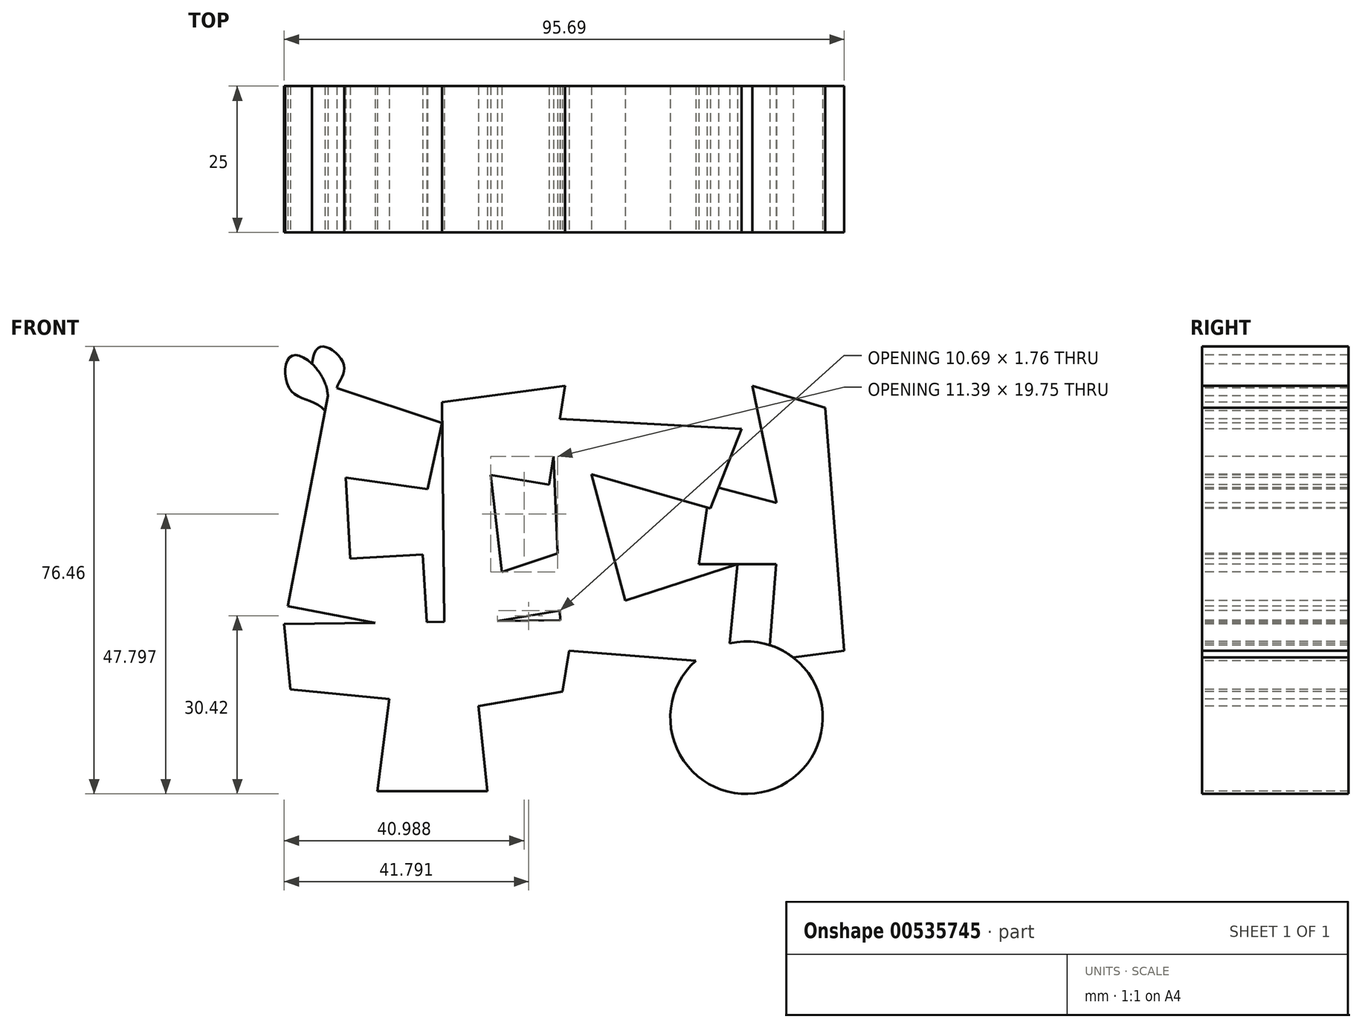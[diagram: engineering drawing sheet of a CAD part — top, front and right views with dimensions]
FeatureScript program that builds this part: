
annotation { "Feature Type Name" : "Feature", "Feature Type Description" : "" }
export const myFeature = defineFeature(function(context is Context, id is Id, definition is map)
    precondition{}
    {
        {
            var Q0;
            Q0=qCreatedBy(makeId("Front.planeOp"),FACE);
            var sketch = newSketch(context, id + "F0", { "sketchPlane" : qUnion([Q0])});
            skLineSegment(sketch, "E0", {"start": v(-48.77, 25.53) * mm, "end": v(-29.6, 19.19) * mm});
            skLineSegment(sketch, "E1", {"start": v(-29.6, 19.19) * mm, "end": v(-32.08, 7.86) * mm});
            skLineSegment(sketch, "E2", {"start": v(-32.08, 7.86) * mm, "end": v(-46.06, 9.88) * mm});
            skLineSegment(sketch, "E3", {"start": v(-46.06, 9.88) * mm, "end": v(-45.24, -3.98) * mm});
            skLineSegment(sketch, "E4", {"start": v(-45.24, -3.98) * mm, "end": v(-32.87, -3.26) * mm});
            skLineSegment(sketch, "E5", {"start": v(-32.87, -3.26) * mm, "end": v(-32.08, -16.68) * mm});
            skLineSegment(sketch, "E6", {"start": v(-32.08, -16.68) * mm, "end": v(-55.94, -12.09) * mm});
            skLineSegment(sketch, "E7", {"start": v(-55.94, -12.09) * mm, "end": v(-48.77, 25.53) * mm});
            skLineSegment(sketch, "E8", {"start": v(-29.6, 22.78) * mm, "end": v(-8.55, 25.53) * mm});
            skLineSegment(sketch, "E9", {"start": v(-8.55, 25.53) * mm, "end": v(-11.3, 8.66) * mm});
            skLineSegment(sketch, "E10", {"start": v(-11.3, 8.66) * mm, "end": v(-21.26, 10.28) * mm});
            skLineSegment(sketch, "E11", {"start": v(-21.26, 10.28) * mm, "end": v(-19.34, -6.27) * mm});
            skLineSegment(sketch, "E12", {"start": v(-19.34, -6.27) * mm, "end": v(-8.5, -2.66) * mm});
            skLineSegment(sketch, "E13", {"start": v(-8.5, -2.66) * mm, "end": v(-9.1, -12.83) * mm});
            skLineSegment(sketch, "E14", {"start": v(-9.1, -12.83) * mm, "end": v(-29.17, -16.15) * mm});
            skLineSegment(sketch, "E15", {"start": v(-29.17, -16.15) * mm, "end": v(-29.6, 22.78) * mm});
            skLineSegment(sketch, "E16", {"start": v(-56.55, -15.18) * mm, "end": v(-7, -14.46) * mm});
            skLineSegment(sketch, "E17", {"start": v(-7, -14.46) * mm, "end": v(-9.02, -26.72) * mm});
            skLineSegment(sketch, "E18", {"start": v(-9.02, -26.72) * mm, "end": v(-23.36, -29.22) * mm});
            skLineSegment(sketch, "E19", {"start": v(-23.36, -29.22) * mm, "end": v(-21.8, -43.75) * mm});
            skLineSegment(sketch, "E20", {"start": v(-21.8, -43.75) * mm, "end": v(-40.65, -43.75) * mm});
            skLineSegment(sketch, "E21", {"start": v(-40.65, -43.75) * mm, "end": v(-38.62, -27.96) * mm});
            skLineSegment(sketch, "E22", {"start": v(-38.62, -27.96) * mm, "end": v(-55.52, -26.34) * mm});
            skLineSegment(sketch, "E23", {"start": v(-55.52, -26.34) * mm, "end": v(-56.55, -15.18) * mm});
            skLineSegment(sketch, "E24", {"start": v(-10.77, 19.93) * mm, "end": v(21.63, 18.2) * mm});
            skLineSegment(sketch, "E25", {"start": v(21.63, 18.2) * mm, "end": v(16.25, 4.58) * mm});
            skLineSegment(sketch, "E26", {"start": v(16.25, 4.58) * mm, "end": v(-4.05, 10.42) * mm});
            skLineSegment(sketch, "E27", {"start": v(-4.05, 10.42) * mm, "end": v(1.7, -11.17) * mm});
            skLineSegment(sketch, "E28", {"start": v(1.7, -11.17) * mm, "end": v(20.91, -4.96) * mm});
            skLineSegment(sketch, "E29", {"start": v(20.91, -4.96) * mm, "end": v(19.26, -21.87) * mm});
            skLineSegment(sketch, "E30", {"start": v(19.26, -21.87) * mm, "end": v(-9.21, -19.65) * mm});
            skLineSegment(sketch, "E31", {"start": v(-9.21, -19.65) * mm, "end": v(-10.77, 19.93) * mm});
            skLineSegment(sketch, "E32", {"start": v(16.25, 8.48) * mm, "end": v(27.6, 5.55) * mm});
            skLineSegment(sketch, "E33", {"start": v(27.6, 5.55) * mm, "end": v(23.43, 25.53) * mm});
            skLineSegment(sketch, "E34", {"start": v(23.43, 25.53) * mm, "end": v(35.87, 21.81) * mm});
            skLineSegment(sketch, "E35", {"start": v(35.87, 21.81) * mm, "end": v(39.14, -19.72) * mm});
            skLineSegment(sketch, "E36", {"start": v(39.14, -19.72) * mm, "end": v(26.22, -21.42) * mm});
            skLineSegment(sketch, "E37", {"start": v(26.22, -21.42) * mm, "end": v(27.51, -4.96) * mm});
            skLineSegment(sketch, "E38", {"start": v(27.51, -4.96) * mm, "end": v(14.3, -4.96) * mm});
            skLineSegment(sketch, "E39", {"start": v(14.3, -4.96) * mm, "end": v(16.25, 8.48) * mm});
            skCircle(sketch, "E40", {"center": v(22.44, -31.17) * mm, "radius": 13.02 * mm});
            skPoint(sketch, "E40.first.point", {"position": v(13.8, -21.44) * mm});
            skPoint(sketch, "E40.second.point", {"position": v(30.77, -41.18) * mm});
            skPoint(sketch, "E40.third.point", {"position": v(35.4, -29.89) * mm});
            skFitSpline(sketch, "E41", {"points": [v(-49.58, 21.3) * mm, v(-55.43, 24.76) * mm, v(-55.25, 30.67) * mm, v(-49.1, 23.85) * mm], "startDerivative": vector(-14.77, 18.4) * mm, "endDerivative": vector(1.75, -32.2) * mm});
            skFitSpline(sketch, "E42", {"points": [v(-49.14, 24.33) * mm, v(-51.56, 26.93) * mm, v(-50.39, 32.21) * mm, v(-46.31, 28.88) * mm, v(-47.66, 24.57) * mm], "startDerivative": vector(-13.77, 8.04) * mm, "endDerivative": vector(-0.25, -17.6) * mm});
            skSolve(sketch);
        }
        {
            var Q0;
            Q0=makeQuery(id+"F0.imprint","IMPRINT",FACE,{"disambiguationData":[TD([[makeQuery(id+"F0.imprint","IMPRINT",EDGE,{"derivedFrom":sQuery(id+"F0.wireOp",EDGE,"E0")}),-1.0]])]});
            var Q1;
            {var subQ1=sQuery(id+"F0.wireOp",EDGE,"E8");Q1=makeQuery(id+"F0.imprint","IMPRINT",FACE,{"disambiguationData":[TD([[makeQuery(id+"F0.imprint","IMPRINT",EDGE,{"derivedFrom":subQ1}),-1.0]])]});}
            var Q2;
            {var subQ0=sQuery(id+"F0.wireOp",EDGE,"E26");var subQ1=sQuery(id+"F0.wireOp",EDGE,"E25");var subQ2=makeQuery(id+"F0.imprint","INTERSECT",VERTEX,{"derivedFrom":[subQ1,subQ0]});Q2=makeQuery(id+"F0.imprint","IMPRINT",FACE,{"disambiguationData":[TD([[makeQuery(id+"F0.imprint","IMPRINT",EDGE,{"disambiguationData":[TD([[subQ2,1.0]])],"derivedFrom":subQ1}),-1.0]])]});}
            var Q3;
            {var subQ0=sQuery(id+"F0.wireOp",EDGE,"E18");Q3=makeQuery(id+"F0.imprint","IMPRINT",FACE,{"disambiguationData":[TD([[makeQuery(id+"F0.imprint","IMPRINT",EDGE,{"derivedFrom":subQ0}),-1.0]])]});}
            var Q4;
            {var subQ0=sQuery(id+"F0.wireOp",EDGE,"E6");var subQ1=sQuery(id+"F0.wireOp",EDGE,"E5");var subQ2=makeQuery(id+"F0.imprint","INTERSECT",VERTEX,{"derivedFrom":[subQ1,subQ0]});Q4=makeQuery(id+"F0.imprint","IMPRINT",FACE,{"disambiguationData":[TD([[makeQuery(id+"F0.imprint","IMPRINT",EDGE,{"disambiguationData":[TD([[subQ2,1.0]])],"derivedFrom":subQ1}),-1.0]])]});}
            var Q5;
            {var subQ0=sQuery(id+"F0.wireOp",EDGE,"E17");var subQ1=sQuery(id+"F0.wireOp",EDGE,"E16");var subQ2=makeQuery(id+"F0.imprint","INTERSECT",VERTEX,{"derivedFrom":[subQ1,subQ0]});Q5=makeQuery(id+"F0.imprint","IMPRINT",FACE,{"disambiguationData":[TD([[makeQuery(id+"F0.imprint","IMPRINT",EDGE,{"disambiguationData":[TD([[subQ2,1.0]])],"derivedFrom":subQ1}),-1.0]])]});}
            var Q6;
            {var subQ0=sQuery(id+"F0.wireOp",EDGE,"E13");Q6=makeQuery(id+"F0.imprint","IMPRINT",FACE,{"disambiguationData":[TD([[makeQuery(id+"F0.imprint","IMPRINT",EDGE,{"derivedFrom":subQ0}),-1.0]])]});}
            var Q7;
            {var subQ0=sQuery(id+"F0.wireOp",EDGE,"E15");var subQ1=sQuery(id+"F0.wireOp",EDGE,"E14");var subQ2=makeQuery(id+"F0.imprint","INTERSECT",VERTEX,{"derivedFrom":[subQ1,subQ0]});Q7=makeQuery(id+"F0.imprint","IMPRINT",FACE,{"disambiguationData":[TD([[makeQuery(id+"F0.imprint","IMPRINT",EDGE,{"disambiguationData":[TD([[subQ2,1.0]])],"derivedFrom":subQ1}),-1.0]])]});}
            var Q8;
            {var subQ5=sQuery(id+"F0.wireOp",EDGE,"E30");var subQ6=sQuery(id+"F0.wireOp",EDGE,"E29");var subQ7=makeQuery(id+"F0.imprint","INTERSECT",VERTEX,{"derivedFrom":[subQ6,subQ5]});Q8=makeQuery(id+"F0.imprint","IMPRINT",FACE,{"disambiguationData":[TD([[makeQuery(id+"F0.imprint","IMPRINT",EDGE,{"disambiguationData":[TD([[subQ7,1.0]])],"derivedFrom":subQ6}),1.0]])]});}
            var Q9;
            {var subQ0=sQuery(id+"F0.wireOp",EDGE,"E30");var subQ1=sQuery(id+"F0.wireOp",EDGE,"E29");var subQ2=makeQuery(id+"F0.imprint","INTERSECT",VERTEX,{"derivedFrom":[subQ1,subQ0]});Q9=makeQuery(id+"F0.imprint","IMPRINT",FACE,{"disambiguationData":[TD([[makeQuery(id+"F0.imprint","IMPRINT",EDGE,{"disambiguationData":[TD([[subQ2,1.0]])],"derivedFrom":subQ1}),-1.0]])]});}
            var Q10;
            {var subQ0=sQuery(id+"F0.wireOp",EDGE,"E37");var subQ1=sQuery(id+"F0.wireOp",EDGE,"E36");var subQ2=makeQuery(id+"F0.imprint","INTERSECT",VERTEX,{"derivedFrom":[subQ1,subQ0]});Q10=makeQuery(id+"F0.imprint","IMPRINT",FACE,{"disambiguationData":[TD([[makeQuery(id+"F0.imprint","IMPRINT",EDGE,{"disambiguationData":[TD([[subQ2,1.0]])],"derivedFrom":subQ1}),-1.0]])]});}
            var Q11;
            {var subQ0=sQuery(id+"F0.wireOp",EDGE,"E24");var subQ1=sQuery(id+"F0.wireOp",EDGE,"E9");var subQ2=makeQuery(id+"F0.imprint","INTERSECT",VERTEX,{"derivedFrom":[subQ1,subQ0]});Q11=makeQuery(id+"F0.imprint","IMPRINT",FACE,{"disambiguationData":[TD([[makeQuery(id+"F0.imprint","IMPRINT",EDGE,{"disambiguationData":[TD([[subQ2,-1.0]])],"derivedFrom":subQ1}),-1.0]])]});}
            var Q12;
            {var subQ11=sQuery(id+"F0.wireOp",EDGE,"E13");Q12=makeQuery(id+"F0.imprint","IMPRINT",FACE,{"disambiguationData":[TD([[makeQuery(id+"F0.imprint","IMPRINT",EDGE,{"derivedFrom":subQ11}),1.0]])]});}
            var Q13;
            {var subQ0=sQuery(id+"F0.wireOp",EDGE,"E7");var subQ1=sQuery(id+"F0.wireOp",EDGE,"E0");var subQ2=makeQuery(id+"F0.imprint","INTERSECT",VERTEX,{"derivedFrom":[subQ1,subQ0]});Q13=makeQuery(id+"F0.imprint","IMPRINT",FACE,{"disambiguationData":[TD([[makeQuery(id+"F0.imprint","IMPRINT",EDGE,{"disambiguationData":[TD([[subQ2,-1.0]])],"derivedFrom":subQ1}),1.0]])]});}
            var Q14;
            {var subQ13=sQuery(id+"F0.wireOp",EDGE,"E1");Q14=makeQuery(id+"F0.imprint","IMPRINT",FACE,{"disambiguationData":[TD([[makeQuery(id+"F0.imprint","IMPRINT",EDGE,{"derivedFrom":subQ13}),-1.0]])]});}
            extrude(context, id + "F1", {"entities" : qUnion([Q0, Q1, Q2, Q3, Q4, Q5, Q6, Q7, Q8, Q9, Q10, Q11, Q12, Q13, Q14]), "oppositeDirection" : true, "depth" : 25 * mm, "offsetDistance" : 25 * mm});
        }
        {
            var Q0;
            {var subQ17=sQuery(id+"F0.wireOp",EDGE,"E33");Q0=makeQuery(id+"F0.imprint","IMPRINT",FACE,{"disambiguationData":[TD([[makeQuery(id+"F0.imprint","IMPRINT",EDGE,{"derivedFrom":subQ17}),-1.0]])]});}
            var Q1;
            {var subQ0=sQuery(id+"F0.wireOp",EDGE,"E41");var subQ1=sQuery(id+"F0.wireOp",EDGE,"E7");var subQ2=makeQuery(id+"F0.imprint","INTERSECT",VERTEX,{"derivedFrom":[subQ1,subQ0]});Q1=makeQuery(id+"F0.imprint","IMPRINT",FACE,{"disambiguationData":[TD([[makeQuery(id+"F0.imprint","IMPRINT",EDGE,{"disambiguationData":[TD([[subQ2,-1.0]])],"derivedFrom":subQ0}),-1.0]])]});}
            var Q2;
            {var subQ0=sQuery(id+"F0.wireOp",EDGE,"02682fb5-d0a3-4bd2-a184-1b8d3688bbf6");var subQ1=sQuery(id+"F0.wireOp",EDGE,"E41");var subQ3=makeQuery(id+"F0.imprint","INTERSECT",VERTEX,{"derivedFrom":[subQ1,subQ0]});Q2=makeQuery(id+"F0.imprint","IMPRINT",FACE,{"disambiguationData":[TD([[makeQuery(id+"F0.imprint","IMPRINT",EDGE,{"disambiguationData":[TD([[subQ3,-1.0]])],"derivedFrom":subQ1}),-1.0]])]});}
            var Q3;
            {var subQ0=sQuery(id+"F0.wireOp",EDGE,"E42");var subQ1=sQuery(id+"F0.wireOp",EDGE,"E41");var subQ2=makeQuery(id+"F0.imprint","INTERSECT",VERTEX,{"disambiguationData":[OD(0.0)],"derivedFrom":[subQ1,subQ0]});Q3=makeQuery(id+"F0.imprint","IMPRINT",FACE,{"disambiguationData":[TD([[makeQuery(id+"F0.imprint","IMPRINT",EDGE,{"disambiguationData":[TD([[subQ2,1.0]])],"derivedFrom":subQ1}),-1.0]])]});}
            extrude(context, id + "F2", {"entities" : qUnion([Q0, Q1, Q2, Q3]), "oppositeDirection" : true, "depth" : 25 * mm, "offsetDistance" : 25 * mm});
        }
    });
